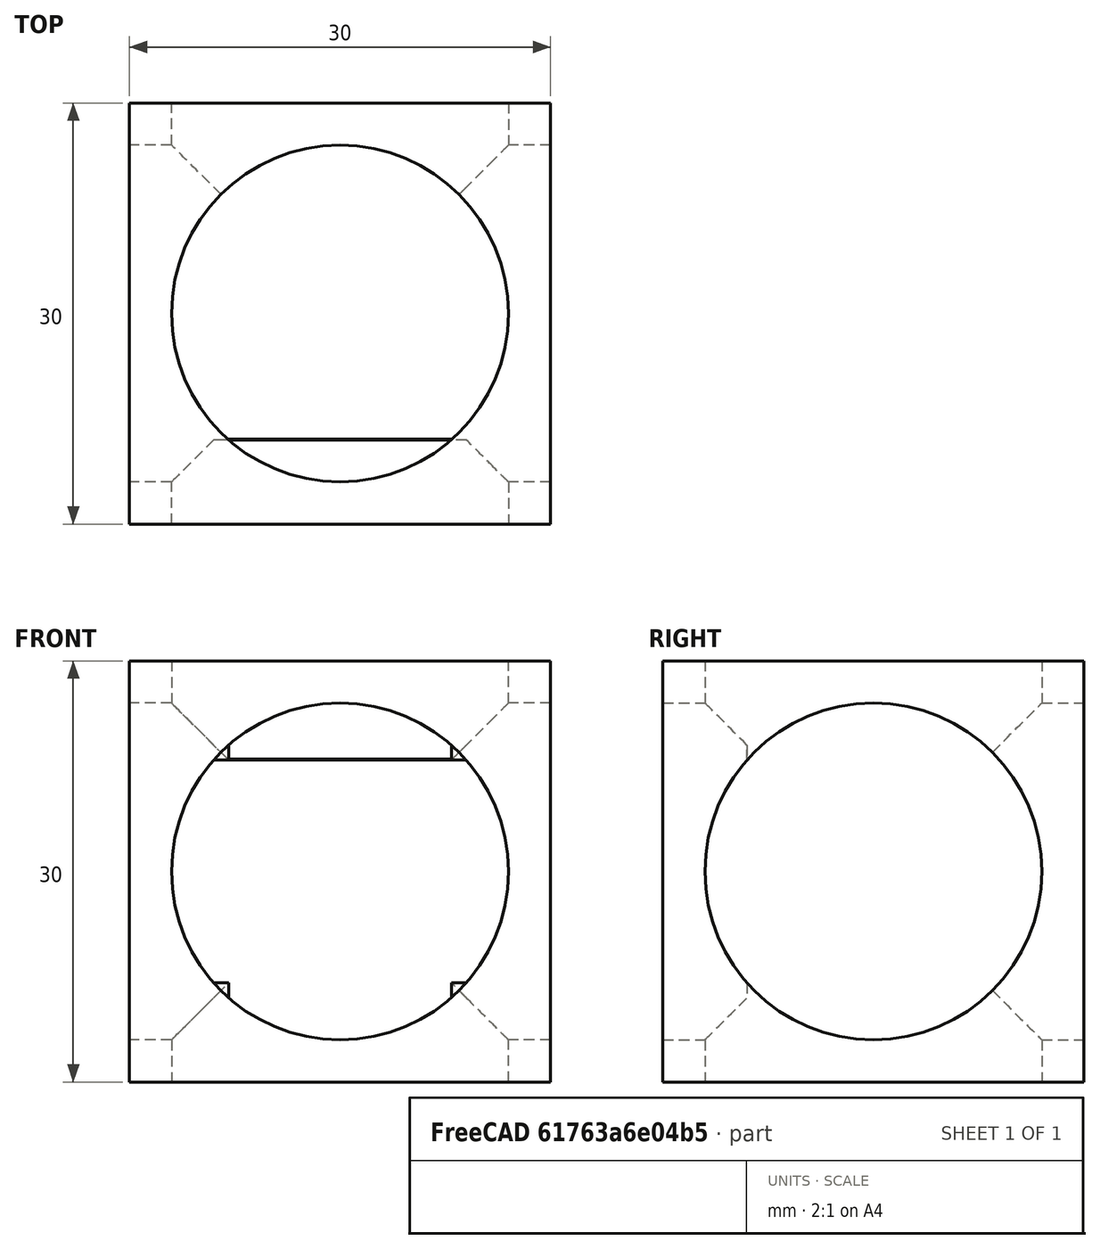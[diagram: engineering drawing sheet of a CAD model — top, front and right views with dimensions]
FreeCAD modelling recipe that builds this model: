
FCSTD DOCUMENT  (FreeCAD 0.21R33694 (Git))
Label: gcasna_repte03
License: All rights reserved
LicenseURL: http://en.wikipedia.org/wiki/All_rights_reserved
objects: Part::Cylinder×6, Part::Box×1, Part::MultiFuse×1, Part::Cut×1, Part::Sphere×1
note: 10 computed .brp shape members not serialized (recipe doc carries the construction recipe); baked Part::Feature solids carry a one-line shape summary decoded from their .brp

FEATURE [Part::Box] Box  label="Cube"
  AttacherType = Attacher::AttachEngine3D
  Height = 30
  Length = 30
  Width = 30
FEATURE [Part::Cylinder] Cylinder
  Angle = 360
  AttacherType = Attacher::AttachEngine3D
  FirstAngle = 0
  Height = 20
  Placement = pos=(24,15,15) rot=(0,1,0;1.5708rad)
  Radius = 12
  SecondAngle = 0
FEATURE [Part::Cylinder] Cylinder001
  Angle = 360
  AttacherType = Attacher::AttachEngine3D
  FirstAngle = 0
  Height = 30
  Placement = pos=(-4,15,15) rot=(0,1,0;1.5708rad)
  Radius = 12
  SecondAngle = 0
FEATURE [Part::Cylinder] Cylinder002
  Angle = 360
  AttacherType = Attacher::AttachEngine3D
  FirstAngle = 0
  Height = 20
  Placement = pos=(15,15,23) rot=(0,0,1;0rad)
  Radius = 12
  SecondAngle = 0
FEATURE [Part::Cylinder] Cylinder003
  Angle = 360
  AttacherType = Attacher::AttachEngine3D
  FirstAngle = 0
  Height = 20
  Placement = pos=(15,15,-3) rot=(0,0,1;0rad)
  Radius = 12
  SecondAngle = 0
FEATURE [Part::Cylinder] Cylinder004
  Angle = 360
  AttacherType = Attacher::AttachEngine3D
  FirstAngle = 0
  Height = 20
  Placement = pos=(15,6,15) rot=(1,0,0;1.5708rad)
  Radius = 12
  SecondAngle = 0
FEATURE [Part::Cylinder] Cylinder005
  Angle = 360
  AttacherType = Attacher::AttachEngine3D
  FirstAngle = 0
  Height = 20
  Placement = pos=(15,34,15) rot=(1,0,0;1.5708rad)
  Radius = 12
  SecondAngle = 0
FEATURE [Part::MultiFuse] Fusion
  Refine = true
  Shapes = -> [Cylinder,Cylinder001,Cylinder002,Cylinder003,Cylinder004,Cylinder005]
FEATURE [Part::Cut] Cut
  Base = -> Box
  Refine = true
  Tool = -> Fusion
FEATURE [Part::Sphere] Sphere
  Angle1 = -90
  Angle2 = 90
  Angle3 = 360
  AttacherType = Attacher::AttachEngine3D
  Placement = pos=(15,15,15) rot=(0,0,1;0rad)
  Radius = 12
